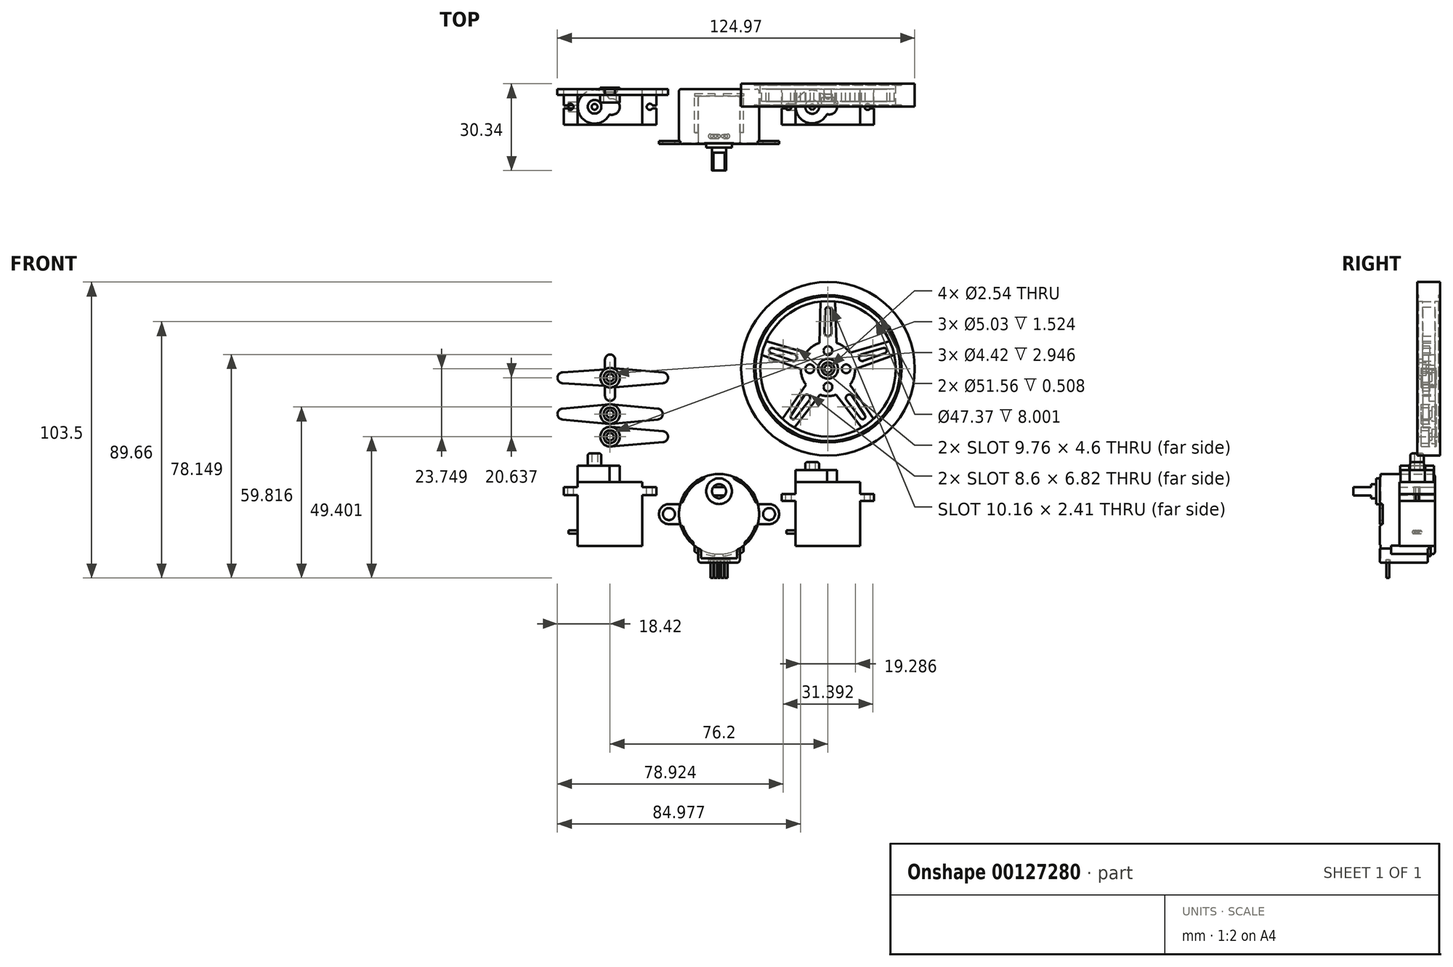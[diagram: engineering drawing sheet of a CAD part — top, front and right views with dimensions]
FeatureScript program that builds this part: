
annotation { "Feature Type Name" : "Feature", "Feature Type Description" : "" }
export const myFeature = defineFeature(function(context is Context, id is Id, definition is map)
    precondition{}
    {
        {
            var Q0;
            Q0=qCreatedBy(makeId("Front.planeOp"),FACE);
            var sketch = newSketch(context, id + "F0", { "sketchPlane" : qUnion([Q0])});
            skCircle(sketch, "E0", {"center": v(0, 0) * mm, "radius": 14 * mm});
            skSolve(sketch);
        }
        {
            var Q0;
            Q0=makeQuery(id+"F0.imprint","IMPRINT",FACE,{"disambiguationData":[TD([[makeQuery(id+"F0.imprint","IMPRINT",EDGE,{"derivedFrom":sQuery(id+"F0.wireOp",EDGE,"E0")}),1.0]])]});
            extrude(context, id + "F1", {"entities" : qUnion([Q0]), "depth" : 19 * mm});
        }
        {
            var Q0;
            Q0=makeQuery(id+"F1.opExtrude","CAP_EDGE",EDGE,{"disambiguationData":[OSD([sQuery(id+"F0.wireOp",EDGE,"E0")])],"isStart":true});
            fillet(context, id + "F2", {"entities" : qUnion([Q0]), "radius" : 0.8 * mm, "tangentPropagation" : true, "allowEdgeOverflow" : false});
        }
        {
            var Q0;
            Q0=makeQuery(id+"F1.opExtrude","CAP_FACE",FACE,{"disambiguationData":[OSD([sQuery(id+"F0.wireOp",EDGE,"E0")])],"isStart":false});
            var sketch = newSketch(context, id + "F3", { "sketchPlane" : qUnion([Q0])});
            skArc(sketch, "E1", {"start": v(12.7, 4.12) * mm, "mid": v(9.8, 9.06) * mm, "end": v(5.12, 12.33) * mm});
            skArc(sketch, "E2", {"start": v(-5.12, 12.33) * mm, "mid": v(-9.8, 9.06) * mm, "end": v(-12.7, 4.13) * mm});
            skLineSegment(sketch, "E3", {"start": v(-5.12, 12.33) * mm, "end": v(-5.12, 13.03) * mm});
            skLineSegment(sketch, "E4", {"start": v(-12.7, 4.12) * mm, "end": v(-13.38, 4.12) * mm});
            skLineSegment(sketch, "E5", {"start": v(12.7, 4.12) * mm, "end": v(13.38, 4.12) * mm});
            skLineSegment(sketch, "E6", {"start": v(5.12, 12.33) * mm, "end": v(5.12, 13.03) * mm});
            skArc(sketch, "E7", {"start": v(-12.7, -4.13) * mm, "mid": v(-11.22, -7.23) * mm, "end": v(-9, -9.86) * mm});
            skArc(sketch, "E8", {"start": v(9, -9.86) * mm, "mid": v(11.22, -7.23) * mm, "end": v(12.7, -4.12) * mm});
            skLineSegment(sketch, "E9", {"start": v(12.7, -4.12) * mm, "end": v(13.38, -4.12) * mm});
            skLineSegment(sketch, "E10", {"start": v(-12.7, -4.13) * mm, "end": v(-13.38, -4.13) * mm});
            skLineSegment(sketch, "E11", {"start": v(-9, -9.86) * mm, "end": v(-9, -10.72) * mm});
            skLineSegment(sketch, "E12", {"start": v(9, -9.86) * mm, "end": v(9, -10.72) * mm});
            skLineSegment(sketch, "E13", {"start": v(13.56, 3.5) * mm, "end": v(17.5, 3.5) * mm});
            skLineSegment(sketch, "E14", {"start": v(13.56, -3.5) * mm, "end": v(17.5, -3.5) * mm});
            skLineSegment(sketch, "E15", {"start": v(-13.56, 3.5) * mm, "end": v(-17.5, 3.5) * mm});
            skLineSegment(sketch, "E16", {"start": v(-13.56, -3.5) * mm, "end": v(-17.5, -3.5) * mm});
            skArc(sketch, "E17", {"start": v(17.5, -3.5) * mm, "mid": v(21, 0) * mm, "end": v(17.5, 3.5) * mm});
            skArc(sketch, "E18", {"start": v(-17.5, 3.5) * mm, "mid": v(-21, 0) * mm, "end": v(-17.5, -3.5) * mm});
            skCircle(sketch, "E19", {"center": v(-17.5, 0) * mm, "radius": 2.1 * mm});
            skCircle(sketch, "E20", {"center": v(17.5, 0) * mm, "radius": 2.1 * mm});
            skCircle(sketch, "E21", {"center": v(0, 8) * mm, "radius": 4.5 * mm});
            skSolve(sketch);
        }
        {
            var Q0;
            {var subQ1=sQuery(id+"F3.wireOp",EDGE,"E15");Q0=makeQuery(id+"F3.imprint","IMPRINT",FACE,{"disambiguationData":[TD([[makeQuery(id+"F3.imprint","IMPRINT",EDGE,{"derivedFrom":subQ1}),1.0]])]});}
            var Q1;
            {var subQ1=sQuery(id+"F3.wireOp",EDGE,"E13");Q1=makeQuery(id+"F3.imprint","IMPRINT",FACE,{"disambiguationData":[TD([[makeQuery(id+"F3.imprint","IMPRINT",EDGE,{"derivedFrom":subQ1}),-1.0]])]});}
            var Q2;
            Q2=makeQuery(id+"F3.imprint","IMPRINT",FACE,{"disambiguationData":[TD([[makeQuery(id+"F3.imprint","IMPRINT",EDGE,{"derivedFrom":sQuery(id+"F3.wireOp",EDGE,"E7")}),-1.0]])]});
            var Q3;
            Q3=makeQuery(id+"F3.imprint","IMPRINT",FACE,{"disambiguationData":[TD([[makeQuery(id+"F3.imprint","IMPRINT",EDGE,{"derivedFrom":sQuery(id+"F3.wireOp",EDGE,"E8")}),-1.0]])]});
            var Q4;
            Q4=makeQuery(id+"F3.imprint","IMPRINT",FACE,{"disambiguationData":[TD([[makeQuery(id+"F3.imprint","IMPRINT",EDGE,{"derivedFrom":sQuery(id+"F3.wireOp",EDGE,"E1")}),-1.0]])]});
            var Q5;
            Q5=makeQuery(id+"F3.imprint","IMPRINT",FACE,{"disambiguationData":[TD([[makeQuery(id+"F3.imprint","IMPRINT",EDGE,{"derivedFrom":sQuery(id+"F3.wireOp",EDGE,"E2")}),-1.0]])]});
            var Q6;
            Q6=makeQuery(id+"F3.imprint","IMPRINT",FACE,{"disambiguationData":[TD([[makeQuery(id+"F3.imprint","IMPRINT",EDGE,{"derivedFrom":sQuery(id+"F3.wireOp",EDGE,"E21")}),1.0]])]});
            extrude(context, id + "F4", {"entities" : qUnion([Q0, Q1, Q2, Q3, Q4, Q5, Q6]), "operationType" : NewBodyOperationType.ADD, "depth" : .25 * mm, "hasSecondDirection" : true, "secondDirectionOppositeDirection" : true, "secondDirectionDepth" : .8 * mm});
        }
        {
            var Q0;
            {var subQ0=sQuery(id+"F0.wireOp",EDGE,"E0");var subQ1=makeQuery(id+"F1.opExtrude","CAP_EDGE",EDGE,{"disambiguationData":[OSD([subQ0])],"isStart":false});Q0=makeQuery(id+"F4.opExtrude","CAP_EDGE",EDGE,{"disambiguationData":[OSD([subQ0]),TDD([makeQuery(id+"F3.imprint","IMPRINT",EDGE,{"disambiguationData":[TD([[makeQuery(id+"F3.imprint","INTERSECT",VERTEX,{"derivedFrom":[subQ1,sQuery(id+"F3.wireOp",EDGE,"E15")]}),-1.0]])],"derivedFrom":subQ1})])],"isStart":false});}
            var Q1;
            {var subQ0=sQuery(id+"F0.wireOp",EDGE,"E0");var subQ1=makeQuery(id+"F1.opExtrude","CAP_EDGE",EDGE,{"disambiguationData":[OSD([subQ0])],"isStart":false});Q1=makeQuery(id+"F4.opExtrude","CAP_EDGE",EDGE,{"disambiguationData":[OSD([subQ0]),TDD([makeQuery(id+"F3.imprint","IMPRINT",EDGE,{"disambiguationData":[TD([[makeQuery(id+"F3.imprint","INTERSECT",VERTEX,{"derivedFrom":[subQ1,sQuery(id+"F3.wireOp",EDGE,"E13")]}),1.0]])],"derivedFrom":subQ1})])],"isStart":false});}
            fillet(context, id + "F5", {"entities" : qUnion([Q0, Q1]), "radius" : 0.25 * mm, "tangentPropagation" : true, "allowEdgeOverflow" : false});
        }
        {
            var Q0;
            Q0=makeQuery(id+"F4.opExtrude","CAP_FACE",FACE,{"disambiguationData":[OSD([sQuery(id+"F3.wireOp",EDGE,"E21")])],"isStart":false});
            extrude(context, id + "F6", {"entities" : qUnion([Q0]), "operationType" : NewBodyOperationType.ADD, "depth" : 1.25 * mm});
        }
        {
            var Q0;
            Q0=makeQuery(id+"F1.opExtrude","CAP_FACE",FACE,{"disambiguationData":[OSD([sQuery(id+"F0.wireOp",EDGE,"E0")])],"isStart":false});
            var sketch = newSketch(context, id + "F7", { "sketchPlane" : qUnion([Q0])});
            skLineSegment(sketch, "E22", {"start": v(-7.25, -11.98) * mm, "end": v(-7.25, -16) * mm});
            skLineSegment(sketch, "E23", {"start": v(-6.25, -17) * mm, "end": v(6.25, -17) * mm});
            skLineSegment(sketch, "E24", {"start": v(7.25, -16) * mm, "end": v(7.25, -11.98) * mm});
            skPoint(sketch, "E25.visualSharp", {"position": v(-7.25, -17) * mm});
            skArc(sketch, "E25.filletArc", {"start": v(-7.25, -16) * mm, "mid": v(-6.96, -16.7) * mm, "end": v(-6.25, -17) * mm});
            skPoint(sketch, "E26.visualSharp", {"position": v(7.25, -17) * mm});
            skArc(sketch, "E26.filletArc", {"start": v(6.25, -17) * mm, "mid": v(6.96, -16.7) * mm, "end": v(7.25, -16) * mm});
            skLineSegment(sketch, "E27.0", {"start": v(-6.25, -15.5) * mm, "end": v(6.25, -15.5) * mm});
            skLineSegment(sketch, "E28.0", {"start": v(-6.25, -12.53) * mm, "end": v(-6.25, -15.5) * mm});
            skLineSegment(sketch, "E29.0", {"start": v(6.25, -15.5) * mm, "end": v(6.25, -12.53) * mm});
            skSolve(sketch);
        }
        {
            var Q0;
            Q0=makeQuery(id+"F7.imprint","IMPRINT",FACE,{"disambiguationData":[TD([[makeQuery(id+"F7.imprint","IMPRINT",EDGE,{"derivedFrom":sQuery(id+"F7.wireOp",EDGE,"E27.0")}),1.0]])]});
            var Q1;
            {var subQ2=sQuery(id+"F7.wireOp",EDGE,"E22");Q1=makeQuery(id+"F7.imprint","IMPRINT",FACE,{"disambiguationData":[TD([[makeQuery(id+"F7.imprint","IMPRINT",EDGE,{"derivedFrom":subQ2}),1.0]])]});}
            extrude(context, id + "F8", {"entities" : qUnion([Q0, Q1]), "operationType" : NewBodyOperationType.ADD, "oppositeDirection" : true, "depth" : 16.5 * mm});
        }
        {
            var Q0;
            {var subQ2=sQuery(id+"F7.wireOp",EDGE,"E22");Q0=makeQuery(id+"F7.imprint","IMPRINT",FACE,{"disambiguationData":[TD([[makeQuery(id+"F7.imprint","IMPRINT",EDGE,{"derivedFrom":subQ2}),1.0]])]});}
            extrude(context, id + "F9", {"entities" : qUnion([Q0]), "operationType" : NewBodyOperationType.ADD, "depth" : .25 * mm});
        }
        {
            var Q0;
            Q0=makeQuery(id+"F8.opExtrude","CAP_FACE",FACE,{"disambiguationData":[OSD([sQuery(id+"F0.wireOp",EDGE,"E0"),sQuery(id+"F7.wireOp",EDGE,"E22"),sQuery(id+"F7.wireOp",EDGE,"E23"),sQuery(id+"F7.wireOp",EDGE,"E24"),sQuery(id+"F7.wireOp",EDGE,"E25.filletArc"),sQuery(id+"F7.wireOp",EDGE,"E26.filletArc")])],"isStart":false});
            var sketch = newSketch(context, id + "F10", { "sketchPlane" : qUnion([Q0])});
            skCircle(sketch, "E30.0", {"center": v(0, 0) * mm, "radius": 14 * mm});
            skLineSegment(sketch, "E31", {"start": v(8.6, -11.05) * mm, "end": v(8.6, -13.05) * mm});
            skLineSegment(sketch, "E32", {"start": v(8.6, -13.05) * mm, "end": v(7.25, -14) * mm});
            skLineSegment(sketch, "E33", {"start": v(-8.6, -11.05) * mm, "end": v(-8.6, -13.05) * mm});
            skLineSegment(sketch, "E34", {"start": v(-8.6, -13.05) * mm, "end": v(-7.25, -14) * mm});
            skPoint(sketch, "E34.endSnap0", {"position": v(-7.25, -13.99) * mm});
            skArc(sketch, "E35", {"start": v(-8.6, -11.98) * mm, "mid": v(-5.23, -13.8) * mm, "end": v(-1.5, -14.67) * mm});
            skArc(sketch, "E36", {"start": v(1.5, -14.67) * mm, "mid": v(5.23, -13.8) * mm, "end": v(8.6, -11.98) * mm});
            skLineSegment(sketch, "E37", {"start": v(-1.5, -14.67) * mm, "end": v(-1.5, -13.92) * mm});
            skLineSegment(sketch, "E38", {"start": v(1.5, -14.67) * mm, "end": v(1.5, -13.92) * mm});
            skSolve(sketch);
        }
        {
            var Q0;
            {var subQ0=sQuery(id+"F10.wireOp",EDGE,"E34");Q0=makeQuery(id+"F10.imprint","IMPRINT",FACE,{"disambiguationData":[TD([[makeQuery(id+"F10.imprint","IMPRINT",EDGE,{"derivedFrom":subQ0}),1.0]])]});}
            var Q1;
            {var subQ0=sQuery(id+"F10.wireOp",EDGE,"E30.0");var subQ3=sQuery(id+"F10.wireOp",EDGE,"E33");var subQ4=makeQuery(id+"F10.imprint","INTERSECT",VERTEX,{"derivedFrom":[subQ0,subQ3]});Q1=makeQuery(id+"F10.imprint","IMPRINT",FACE,{"disambiguationData":[TD([[makeQuery(id+"F10.imprint","IMPRINT",EDGE,{"disambiguationData":[TD([[subQ4,-1.0]])],"derivedFrom":subQ0}),-1.0]])]});}
            var Q2;
            {var subQ0=sQuery(id+"F10.wireOp",EDGE,"E32");Q2=makeQuery(id+"F10.imprint","IMPRINT",FACE,{"disambiguationData":[TD([[makeQuery(id+"F10.imprint","IMPRINT",EDGE,{"derivedFrom":subQ0}),-1.0]])]});}
            var Q3;
            {var subQ0=sQuery(id+"F10.wireOp",EDGE,"E30.0");var subQ3=sQuery(id+"F10.wireOp",EDGE,"E31");var subQ4=makeQuery(id+"F10.imprint","INTERSECT",VERTEX,{"derivedFrom":[subQ0,subQ3]});Q3=makeQuery(id+"F10.imprint","IMPRINT",FACE,{"disambiguationData":[TD([[makeQuery(id+"F10.imprint","IMPRINT",EDGE,{"disambiguationData":[TD([[subQ4,1.0]])],"derivedFrom":subQ0}),-1.0]])]});}
            extrude(context, id + "F11", {"entities" : qUnion([Q0, Q1, Q2, Q3]), "operationType" : NewBodyOperationType.ADD, "oppositeDirection" : true, "depth" : 12.75 * mm});
        }
        {
            var Q0;
            {var subQ3=sQuery(id+"F10.wireOp",EDGE,"E37");Q0=makeQuery(id+"F10.imprint","IMPRINT",FACE,{"disambiguationData":[TD([[makeQuery(id+"F10.imprint","IMPRINT",EDGE,{"derivedFrom":subQ3}),1.0]])]});}
            var Q1;
            {var subQ0=sQuery(id+"F10.wireOp",EDGE,"E30.0");var subQ3=sQuery(id+"F10.wireOp",EDGE,"E33");var subQ4=makeQuery(id+"F10.imprint","INTERSECT",VERTEX,{"derivedFrom":[subQ0,subQ3]});Q1=makeQuery(id+"F10.imprint","IMPRINT",FACE,{"disambiguationData":[TD([[makeQuery(id+"F10.imprint","IMPRINT",EDGE,{"disambiguationData":[TD([[subQ4,-1.0]])],"derivedFrom":subQ0}),-1.0]])]});}
            var Q2;
            {var subQ3=sQuery(id+"F10.wireOp",EDGE,"E38");Q2=makeQuery(id+"F10.imprint","IMPRINT",FACE,{"disambiguationData":[TD([[makeQuery(id+"F10.imprint","IMPRINT",EDGE,{"derivedFrom":subQ3}),-1.0]])]});}
            var Q3;
            {var subQ0=sQuery(id+"F10.wireOp",EDGE,"E30.0");var subQ3=sQuery(id+"F10.wireOp",EDGE,"E31");var subQ4=makeQuery(id+"F10.imprint","INTERSECT",VERTEX,{"derivedFrom":[subQ0,subQ3]});Q3=makeQuery(id+"F10.imprint","IMPRINT",FACE,{"disambiguationData":[TD([[makeQuery(id+"F10.imprint","IMPRINT",EDGE,{"disambiguationData":[TD([[subQ4,1.0]])],"derivedFrom":subQ0}),-1.0]])]});}
            extrude(context, id + "F12", {"entities" : qUnion([Q0, Q1, Q2, Q3]), "operationType" : NewBodyOperationType.ADD, "depth" : 1 * mm});
        }
        {
            var Q0;
            Q0=makeQuery(id+"F11.opExtrude","SWEPT_EDGE",EDGE,{"disambiguationData":[OSD([sQuery(id+"F10.wireOp",EDGE,"E33"),sQuery(id+"F10.wireOp",EDGE,"E34")])]});
            var Q1;
            Q1=makeQuery(id+"F11.opExtrude","SWEPT_EDGE",EDGE,{"disambiguationData":[OSD([sQuery(id+"F10.wireOp",EDGE,"E31"),sQuery(id+"F10.wireOp",EDGE,"E32")])]});
            var Q2;
            Q2=makeQuery(id+"F8.opExtrude","CAP_EDGE",EDGE,{"disambiguationData":[OSD([sQuery(id+"F7.wireOp",EDGE,"E23")])],"isStart":false});
            var Q3;
            Q3=makeQuery(id+"F9.opExtrude","CAP_EDGE",EDGE,{"disambiguationData":[OSD([sQuery(id+"F7.wireOp",EDGE,"E23")])],"isStart":false});
            fillet(context, id + "F13", {"entities" : qUnion([Q0, Q1, Q2, Q3]), "radius" : .5 * mm, "tangentPropagation" : true, "allowEdgeOverflow" : false});
        }
        {
            var Q0;
            Q0=makeQuery(id+"F6.opExtrude","CAP_FACE",FACE,{"disambiguationData":[OSD([sQuery(id+"F3.wireOp",EDGE,"E21")])],"isStart":false});
            var sketch = newSketch(context, id + "F14", { "sketchPlane" : qUnion([Q0])});
            skCircle(sketch, "E39", {"center": v(0, 8) * mm, "radius": 2.48 * mm});
            skLineSegment(sketch, "E40", {"start": v(-1.99, 9.48) * mm, "end": v(1.99, 9.48) * mm});
            skLineSegment(sketch, "E41", {"start": v(-1.99, 6.53) * mm, "end": v(1.99, 6.53) * mm});
            skSolve(sketch);
        }
        {
            var Q0;
            Q0=makeQuery(id+"F14.imprint","IMPRINT",FACE,{"disambiguationData":[TD([[makeQuery(id+"F14.imprint","IMPRINT",EDGE,{"derivedFrom":sQuery(id+"F14.wireOp",EDGE,"E39")}),1.0]])]});
            var Q1;
            {var subQ0=sQuery(id+"F14.wireOp",EDGE,"E41");Q1=makeQuery(id+"F14.imprint","IMPRINT",FACE,{"disambiguationData":[TD([[makeQuery(id+"F14.imprint","IMPRINT",EDGE,{"derivedFrom":subQ0}),-1.0]])]});}
            var Q2;
            {var subQ0=sQuery(id+"F14.wireOp",EDGE,"E40");Q2=makeQuery(id+"F14.imprint","IMPRINT",FACE,{"disambiguationData":[TD([[makeQuery(id+"F14.imprint","IMPRINT",EDGE,{"derivedFrom":subQ0}),1.0]])]});}
            extrude(context, id + "F15", {"entities" : qUnion([Q0, Q1, Q2]), "operationType" : NewBodyOperationType.ADD, "depth" : 1.75 * mm});
        }
        {
            var Q0;
            {var subQ0=sQuery(id+"F14.wireOp",EDGE,"E40");Q0=makeQuery(id+"F14.imprint","IMPRINT",FACE,{"disambiguationData":[TD([[makeQuery(id+"F14.imprint","IMPRINT",EDGE,{"derivedFrom":subQ0}),-1.0]])]});}
            extrude(context, id + "F16", {"entities" : qUnion([Q0]), "operationType" : NewBodyOperationType.ADD, "depth" : 8 * mm});
        }
        {
            var Q0;
            {var subQ0=sQuery(id+"F7.wireOp",EDGE,"E23");Q0=makeQuery(id+"F9.boolean.opBoolean","MERGE",FACE,{"derivedFrom":[makeQuery(id+"F8.opExtrude","SWEPT_FACE",FACE,{"disambiguationData":[OSD([subQ0])]}),makeQuery(id+"F9.opExtrude","SWEPT_FACE",FACE,{"disambiguationData":[OSD([subQ0])]})]});}
            var sketch = newSketch(context, id + "F17", { "sketchPlane" : qUnion([Q0])});
            skLineSegment(sketch, "E42", {"start": v(-3, 15.75) * mm, "end": v(3, 15.75) * mm});
            skLineSegment(sketch, "E43", {"start": v(-3, 17.25) * mm, "end": v(3, 17.25) * mm});
            skArc(sketch, "E44", {"start": v(-3, 17.25) * mm, "mid": v(-3.75, 16.5) * mm, "end": v(-3, 15.75) * mm});
            skArc(sketch, "E45", {"start": v(3, 15.75) * mm, "mid": v(3.75, 16.5) * mm, "end": v(3, 17.25) * mm});
            skLineSegment(sketch, "E46", {"start": v(-3, 16.5) * mm, "end": v(3, 16.5) * mm, "construction": true});
            skPoint(sketch, "E47", {"position": v(0, 16.5) * mm});
            skSolve(sketch);
        }
        {
            var Q0;
            Q0=makeQuery(id+"F17.imprint","IMPRINT",FACE,{"disambiguationData":[TD([[makeQuery(id+"F17.imprint","IMPRINT",EDGE,{"derivedFrom":sQuery(id+"F17.wireOp",EDGE,"E42")}),1.0]])]});
            extrude(context, id + "F18", {"entities" : qUnion([Q0]), "operationType" : NewBodyOperationType.REMOVE, "oppositeDirection" : true, "depth" : 1 * mm});
        }
        {
            var Q0;
            Q0=makeQuery(id+"F18.boolean.opBoolean","COPY",FACE,{"derivedFrom":makeQuery(id+"F18.opExtrude","CAP_FACE",FACE,{"disambiguationData":[OSD([sQuery(id+"F17.wireOp",EDGE,"E42"),sQuery(id+"F17.wireOp",EDGE,"E43"),sQuery(id+"F17.wireOp",EDGE,"E44"),sQuery(id+"F17.wireOp",EDGE,"E45")])],"isStart":false})});
            var sketch = newSketch(context, id + "F19", { "sketchPlane" : qUnion([Q0])});
            skLineSegment(sketch, "E48", {"start": v(-3, 16.5) * mm, "end": v(3, 16.5) * mm, "construction": true});
            skCircle(sketch, "E49", {"center": v(-2.5, 16.5) * mm, "radius": 0.5 * mm});
            skCircle(sketch, "E50", {"center": v(2.5, 16.5) * mm, "radius": 0.5 * mm});
            skCircle(sketch, "E51", {"center": v(0, 16.5) * mm, "radius": 0.5 * mm});
            skLineSegment(sketch, "E52", {"start": v(-2.5, 16.5) * mm, "end": v(0, 16.5) * mm, "construction": true});
            skLineSegment(sketch, "E53", {"start": v(0, 16.5) * mm, "end": v(2.5, 16.5) * mm, "construction": true});
            skCircle(sketch, "E54", {"center": v(-1.25, 16.5) * mm, "radius": 0.5 * mm});
            skCircle(sketch, "E55", {"center": v(1.25, 16.5) * mm, "radius": 0.5 * mm});
            skSolve(sketch);
        }
        {
            var Q0;
            Q0=makeQuery(id+"F19.imprint","IMPRINT",FACE,{"disambiguationData":[TD([[makeQuery(id+"F19.imprint","IMPRINT",EDGE,{"derivedFrom":sQuery(id+"F19.wireOp",EDGE,"E49")}),1.0]])]});
            var Q1;
            Q1=makeQuery(id+"F19.imprint","IMPRINT",FACE,{"disambiguationData":[TD([[makeQuery(id+"F19.imprint","IMPRINT",EDGE,{"derivedFrom":sQuery(id+"F19.wireOp",EDGE,"E54")}),1.0]])]});
            var Q2;
            Q2=makeQuery(id+"F19.imprint","IMPRINT",FACE,{"disambiguationData":[TD([[makeQuery(id+"F19.imprint","IMPRINT",EDGE,{"derivedFrom":sQuery(id+"F19.wireOp",EDGE,"E51")}),1.0]])]});
            var Q3;
            Q3=makeQuery(id+"F19.imprint","IMPRINT",FACE,{"disambiguationData":[TD([[makeQuery(id+"F19.imprint","IMPRINT",EDGE,{"derivedFrom":sQuery(id+"F19.wireOp",EDGE,"E55")}),1.0]])]});
            var Q4;
            Q4=makeQuery(id+"F19.imprint","IMPRINT",FACE,{"disambiguationData":[TD([[makeQuery(id+"F19.imprint","IMPRINT",EDGE,{"derivedFrom":sQuery(id+"F19.wireOp",EDGE,"E50")}),1.0]])]});
            extrude(context, id + "F20", {"entities" : qUnion([Q0, Q1, Q2, Q3, Q4]), "operationType" : NewBodyOperationType.ADD, "depth" : 6.35 * mm});
        }
        {
            var Q0;
            Q0=qCreatedBy(makeId("Front.planeOp"),FACE);
            var sketch = newSketch(context, id + "F21", { "sketchPlane" : qUnion([Q0])});
            skLineSegment(sketch, "E56.bottom", {"start": v(26.8, -11.18) * mm, "end": v(49.4, -11.18) * mm});
            skLineSegment(sketch, "E56.top", {"start": v(26.8, 11.18) * mm, "end": v(49.4, 11.18) * mm});
            skLineSegment(sketch, "E56.left", {"start": v(26.8, -11.18) * mm, "end": v(26.8, 11.18) * mm});
            skLineSegment(sketch, "E56.right", {"start": v(49.4, -11.18) * mm, "end": v(49.4, 11.18) * mm});
            skPoint(sketch, "E56.middle", {"position": v(38.1, 0) * mm});
            skLineSegment(sketch, "E57.bottom", {"start": v(21.97, 4.57) * mm, "end": v(54.23, 4.57) * mm});
            skLineSegment(sketch, "E57.top", {"start": v(21.97, 6.99) * mm, "end": v(54.23, 6.99) * mm});
            skLineSegment(sketch, "E57.left", {"start": v(21.97, 4.57) * mm, "end": v(21.97, 6.99) * mm});
            skLineSegment(sketch, "E57.right", {"start": v(54.23, 4.57) * mm, "end": v(54.23, 6.99) * mm});
            skPoint(sketch, "E57.middle", {"position": v(38.1, 5.78) * mm});
            skLineSegment(sketch, "E58.bottom", {"start": v(-26.8, -11.18) * mm, "end": v(-49.4, -11.18) * mm});
            skLineSegment(sketch, "E58.top", {"start": v(-26.8, 11.18) * mm, "end": v(-49.4, 11.18) * mm});
            skLineSegment(sketch, "E58.left", {"start": v(-26.8, -11.18) * mm, "end": v(-26.8, 11.18) * mm});
            skLineSegment(sketch, "E58.right", {"start": v(-49.4, -11.18) * mm, "end": v(-49.4, 11.18) * mm});
            skPoint(sketch, "E58.middle", {"position": v(-38.1, 0) * mm});
            skLineSegment(sketch, "E59.bottom", {"start": v(-54.27, 6.68) * mm, "end": v(-21.93, 6.68) * mm});
            skLineSegment(sketch, "E59.top", {"start": v(-54.27, 9.4) * mm, "end": v(-21.93, 9.4) * mm});
            skLineSegment(sketch, "E59.left", {"start": v(-54.27, 6.68) * mm, "end": v(-54.27, 9.4) * mm});
            skLineSegment(sketch, "E59.right", {"start": v(-21.93, 6.68) * mm, "end": v(-21.93, 9.4) * mm});
            skPoint(sketch, "E59.middle", {"position": v(-38.1, 8.04) * mm});
            skSolve(sketch);
        }
        {
            var Q0;
            {var subQ0=sQuery(id+"F21.wireOp",EDGE,"E56.top");Q0=makeQuery(id+"F21.imprint","IMPRINT",FACE,{"disambiguationData":[TD([[makeQuery(id+"F21.imprint","IMPRINT",EDGE,{"derivedFrom":subQ0}),-1.0]])]});}
            var Q1;
            {var subQ0=sQuery(id+"F21.wireOp",EDGE,"E57.bottom");var subQ1=sQuery(id+"F21.wireOp",EDGE,"E56.left");var subQ2=makeQuery(id+"F21.imprint","INTERSECT",VERTEX,{"derivedFrom":[subQ1,subQ0]});Q1=makeQuery(id+"F21.imprint","IMPRINT",FACE,{"disambiguationData":[TD([[makeQuery(id+"F21.imprint","IMPRINT",EDGE,{"disambiguationData":[TD([[subQ2,-1.0]])],"derivedFrom":subQ1}),-1.0]])]});}
            var Q2;
            {var subQ5=sQuery(id+"F21.wireOp",EDGE,"E57.left");Q2=makeQuery(id+"F21.imprint","IMPRINT",FACE,{"disambiguationData":[TD([[makeQuery(id+"F21.imprint","IMPRINT",EDGE,{"derivedFrom":subQ5}),-1.0]])]});}
            var Q3;
            {var subQ0=sQuery(id+"F21.wireOp",EDGE,"E56.bottom");Q3=makeQuery(id+"F21.imprint","IMPRINT",FACE,{"disambiguationData":[TD([[makeQuery(id+"F21.imprint","IMPRINT",EDGE,{"derivedFrom":subQ0}),1.0]])]});}
            var Q4;
            {var subQ5=sQuery(id+"F21.wireOp",EDGE,"E57.right");Q4=makeQuery(id+"F21.imprint","IMPRINT",FACE,{"disambiguationData":[TD([[makeQuery(id+"F21.imprint","IMPRINT",EDGE,{"derivedFrom":subQ5}),1.0]])]});}
            var Q5;
            {var subQ0=sQuery(id+"F21.wireOp",EDGE,"E58.bottom");Q5=makeQuery(id+"F21.imprint","IMPRINT",FACE,{"disambiguationData":[TD([[makeQuery(id+"F21.imprint","IMPRINT",EDGE,{"derivedFrom":subQ0}),-1.0]])]});}
            var Q6;
            {var subQ0=sQuery(id+"F21.wireOp",EDGE,"E59.bottom");var subQ1=sQuery(id+"F21.wireOp",EDGE,"E58.left");var subQ2=makeQuery(id+"F21.imprint","INTERSECT",VERTEX,{"derivedFrom":[subQ1,subQ0]});Q6=makeQuery(id+"F21.imprint","IMPRINT",FACE,{"disambiguationData":[TD([[makeQuery(id+"F21.imprint","IMPRINT",EDGE,{"disambiguationData":[TD([[subQ2,-1.0]])],"derivedFrom":subQ1}),1.0]])]});}
            var Q7;
            {var subQ5=sQuery(id+"F21.wireOp",EDGE,"E59.right");Q7=makeQuery(id+"F21.imprint","IMPRINT",FACE,{"disambiguationData":[TD([[makeQuery(id+"F21.imprint","IMPRINT",EDGE,{"derivedFrom":subQ5}),1.0]])]});}
            var Q8;
            {var subQ5=sQuery(id+"F21.wireOp",EDGE,"E59.left");Q8=makeQuery(id+"F21.imprint","IMPRINT",FACE,{"disambiguationData":[TD([[makeQuery(id+"F21.imprint","IMPRINT",EDGE,{"derivedFrom":subQ5}),-1.0]])]});}
            var Q9;
            {var subQ0=sQuery(id+"F21.wireOp",EDGE,"E58.top");Q9=makeQuery(id+"F21.imprint","IMPRINT",FACE,{"disambiguationData":[TD([[makeQuery(id+"F21.imprint","IMPRINT",EDGE,{"derivedFrom":subQ0}),1.0]])]});}
            extrude(context, id + "F22", {"entities" : qUnion([Q0, Q1, Q2, Q3, Q4, Q5, Q6, Q7, Q8, Q9]), "depth" : 12.45 * mm});
        }
        {
            var Q0;
            {var subQ0=sQuery(id+"F21.wireOp",EDGE,"E57.top");Q0=makeQuery(id+"F22.opExtrude","SWEPT_FACE",FACE,{"disambiguationData":[OSD([subQ0]),TDD([makeQuery(id+"F21.imprint","IMPRINT",EDGE,{"disambiguationData":[TD([[makeQuery(id+"F21.imprint","INTERSECT",VERTEX,{"derivedFrom":[subQ0,sQuery(id+"F21.wireOp",EDGE,"E57.left")]}),-1.0]])],"derivedFrom":subQ0})])]});}
            var sketch = newSketch(context, id + "F23", { "sketchPlane" : qUnion([Q0])});
            skLineSegment(sketch, "E60.0.0", {"start": v(54.23, 0) * mm, "end": v(49.4, 0) * mm, "construction": true});
            skLineSegment(sketch, "E60.0.1", {"start": v(49.4, 0) * mm, "end": v(49.4, -12.45) * mm, "construction": true});
            skLineSegment(sketch, "E60.0.2", {"start": v(49.4, -12.45) * mm, "end": v(54.23, -12.45) * mm, "construction": true});
            skLineSegment(sketch, "E60.0.3", {"start": v(54.23, -12.45) * mm, "end": v(54.23, 0) * mm, "construction": true});
            skArc(sketch, "E61", {"start": v(23.3, -6.73) * mm, "mid": v(25.34, -6.22) * mm, "end": v(23.3, -5.71) * mm});
            skPoint(sketch, "E61.centerSnap0", {"position": v(26.8, -6.22) * mm});
            skArc(sketch, "E62", {"start": v(52.9, -5.72) * mm, "mid": v(50.86, -6.22) * mm, "end": v(52.9, -6.73) * mm});
            skPoint(sketch, "E62.centerSnap0", {"position": v(54.23, -6.22) * mm});
            skLineSegment(sketch, "E63", {"start": v(23.3, -5.71) * mm, "end": v(21.97, -5.71) * mm});
            skLineSegment(sketch, "E64", {"start": v(23.3, -6.73) * mm, "end": v(21.97, -6.73) * mm});
            skLineSegment(sketch, "E65", {"start": v(52.9, -5.72) * mm, "end": v(54.23, -5.72) * mm});
            skLineSegment(sketch, "E66", {"start": v(54.23, -5.72) * mm, "end": v(54.23, -6.73) * mm});
            skLineSegment(sketch, "E67", {"start": v(54.23, -6.73) * mm, "end": v(52.9, -6.73) * mm});
            skSolve(sketch);
        }
        {
            var Q0;
            Q0=makeQuery(id+"F23.imprint","IMPRINT",FACE,{"disambiguationData":[TD([[makeQuery(id+"F23.imprint","IMPRINT",EDGE,{"derivedFrom":sQuery(id+"F23.wireOp",EDGE,"E61")}),1.0]])]});
            var Q1;
            Q1=makeQuery(id+"F23.imprint","IMPRINT",FACE,{"disambiguationData":[TD([[makeQuery(id+"F23.imprint","IMPRINT",EDGE,{"derivedFrom":sQuery(id+"F23.wireOp",EDGE,"E62")}),1.0]])]});
            extrude(context, id + "F24", {"entities" : qUnion([Q0, Q1]), "operationType" : NewBodyOperationType.REMOVE, "oppositeDirection" : true, "depth" : 3.17 * mm});
        }
        {
            var Q0;
            Q0=makeQuery(id+"F22.opExtrude","SWEPT_FACE",FACE,{"disambiguationData":[OSD([sQuery(id+"F21.wireOp",EDGE,"E56.top")])]});
            var sketch = newSketch(context, id + "F25", { "sketchPlane" : qUnion([Q0])});
            skCircle(sketch, "E68", {"center": v(32.58, -6.22) * mm, "radius": 5.78 * mm});
            skArc(sketch, "E69", {"start": v(37.77, -8.75) * mm, "mid": v(41.27, -6.22) * mm, "end": v(37.77, -3.7) * mm});
            skPoint(sketch, "E70", {"position": v(26.8, -6.22) * mm});
            skLineSegment(sketch, "E71.0", {"start": v(-49.4, -12.45) * mm, "end": v(-49.4, 0) * mm, "construction": true});
            skCircle(sketch, "E72", {"center": v(-43.52, -6.22) * mm, "radius": 5.88 * mm});
            skPoint(sketch, "E72.centerSnap0", {"position": v(-49.4, -6.22) * mm});
            skArc(sketch, "E73", {"start": v(-38.3, -8.9) * mm, "mid": v(-34.72, -6.22) * mm, "end": v(-38.3, -3.54) * mm});
            skSolve(sketch);
        }
        {
            var Q0;
            {var subQ0=sQuery(id+"F25.wireOp",EDGE,"E69");var subQ1=sQuery(id+"F25.wireOp",EDGE,"E68");var subQ4=makeQuery(id+"F25.imprint","INTERSECT",VERTEX,{"disambiguationData":[OD(0.0)],"derivedFrom":[subQ1,subQ0]});Q0=makeQuery(id+"F25.imprint","IMPRINT",FACE,{"disambiguationData":[TD([[makeQuery(id+"F25.imprint","IMPRINT",EDGE,{"disambiguationData":[TD([[subQ4,-1.0]])],"derivedFrom":subQ1}),1.0]])]});}
            var Q1;
            {var subQ0=sQuery(id+"F25.wireOp",EDGE,"E69");Q1=makeQuery(id+"F25.imprint","IMPRINT",FACE,{"disambiguationData":[TD([[makeQuery(id+"F25.imprint","IMPRINT",EDGE,{"derivedFrom":subQ0}),1.0]])]});}
            extrude(context, id + "F26", {"entities" : qUnion([Q0, Q1]), "operationType" : NewBodyOperationType.ADD, "depth" : 4.22 * mm});
        }
        {
            var Q0;
            Q0=makeQuery(id+"F26.opExtrude","CAP_FACE",FACE,{"disambiguationData":[OSD([sQuery(id+"F25.wireOp",EDGE,"E68"),sQuery(id+"F25.wireOp",EDGE,"E69")])],"isStart":false});
            var sketch = newSketch(context, id + "F27", { "sketchPlane" : qUnion([Q0])});
            skCircle(sketch, "E74", {"center": v(32.58, -6.22) * mm, "radius": 2.44 * mm});
            skCircle(sketch, "E75", {"center": v(32.58, -6.22) * mm, "radius": 1 * mm});
            skSolve(sketch);
        }
        {
            var Q0;
            Q0=makeQuery(id+"F27.imprint","IMPRINT",FACE,{"disambiguationData":[TD([[makeQuery(id+"F27.imprint","IMPRINT",EDGE,{"derivedFrom":sQuery(id+"F27.wireOp",EDGE,"E74")}),1.0]])]});
            extrude(context, id + "F28", {"entities" : qUnion([Q0]), "operationType" : NewBodyOperationType.ADD, "depth" : 2.8 * mm});
        }
        {
            var Q0;
            {var subQ0=sQuery(id+"F21.wireOp",EDGE,"E56.left");Q0=makeQuery(id+"F22.opExtrude","SWEPT_FACE",FACE,{"disambiguationData":[OSD([subQ0]),TDD([makeQuery(id+"F21.imprint","IMPRINT",EDGE,{"disambiguationData":[TD([[makeQuery(id+"F21.imprint","INTERSECT",VERTEX,{"derivedFrom":[sQuery(id+"F21.wireOp",EDGE,"E56.bottom"),subQ0]}),-1.0]])],"derivedFrom":subQ0})])]});}
            var sketch = newSketch(context, id + "F29", { "sketchPlane" : qUnion([Q0])});
            skCircle(sketch, "E76", {"center": v(6.8, -6.3) * mm, "radius": 0.56 * mm});
            skCircle(sketch, "E77", {"center": v(5.65, -6.3) * mm, "radius": 0.56 * mm});
            skLineSegment(sketch, "E78", {"start": v(5.65, -6.3) * mm, "end": v(6.8, -6.3) * mm, "construction": true});
            skPoint(sketch, "E79", {"position": v(6.22, -11.18) * mm});
            skPoint(sketch, "E80", {"position": v(6.22, -6.3) * mm});
            skSolve(sketch);
        }
        {
            var Q0;
            Q0=makeQuery(id+"F29.imprint","IMPRINT",FACE,{"disambiguationData":[TD([[makeQuery(id+"F29.imprint","IMPRINT",EDGE,{"derivedFrom":sQuery(id+"F29.wireOp",EDGE,"E77")}),1.0]])]});
            var Q1;
            Q1=makeQuery(id+"F29.imprint","IMPRINT",FACE,{"disambiguationData":[TD([[makeQuery(id+"F29.imprint","IMPRINT",EDGE,{"derivedFrom":sQuery(id+"F29.wireOp",EDGE,"E76")}),1.0]])]});
            extrude(context, id + "F30", {"entities" : qUnion([Q0, Q1]), "operationType" : NewBodyOperationType.ADD, "depth" : 3.17 * mm});
        }
        {
            var Q0;
            {var subQ0=sQuery(id+"F21.wireOp",EDGE,"E59.top");Q0=makeQuery(id+"F22.opExtrude","SWEPT_FACE",FACE,{"disambiguationData":[OSD([subQ0]),TDD([makeQuery(id+"F21.imprint","IMPRINT",EDGE,{"disambiguationData":[TD([[makeQuery(id+"F21.imprint","INTERSECT",VERTEX,{"derivedFrom":[subQ0,sQuery(id+"F21.wireOp",EDGE,"E59.left")]}),-1.0]])],"derivedFrom":subQ0})])]});}
            var sketch = newSketch(context, id + "F31", { "sketchPlane" : qUnion([Q0])});
            skArc(sketch, "E81", {"start": v(-52.93, -6.73) * mm, "mid": v(-50.9, -6.22) * mm, "end": v(-52.93, -5.72) * mm});
            skPoint(sketch, "E81.centerSnap0", {"position": v(-49.4, -6.22) * mm});
            skArc(sketch, "E82", {"start": v(-23.27, -5.72) * mm, "mid": v(-25.3, -6.22) * mm, "end": v(-23.27, -6.73) * mm});
            skPoint(sketch, "E82.centerSnap0", {"position": v(-21.93, -6.22) * mm});
            skLineSegment(sketch, "E83", {"start": v(-52.93, -5.72) * mm, "end": v(-54.27, -5.72) * mm});
            skLineSegment(sketch, "E84", {"start": v(-52.93, -6.73) * mm, "end": v(-54.27, -6.73) * mm});
            skLineSegment(sketch, "E85", {"start": v(-23.27, -5.72) * mm, "end": v(-21.93, -5.72) * mm});
            skLineSegment(sketch, "E86", {"start": v(-21.93, -5.72) * mm, "end": v(-21.93, -6.73) * mm});
            skLineSegment(sketch, "E87", {"start": v(-21.93, -6.73) * mm, "end": v(-23.27, -6.73) * mm});
            skLineSegment(sketch, "E88.0.0", {"start": v(-21.93, 0) * mm, "end": v(-26.8, 0) * mm, "construction": true});
            skLineSegment(sketch, "E88.0.1", {"start": v(-26.8, 0) * mm, "end": v(-26.8, -12.45) * mm, "construction": true});
            skLineSegment(sketch, "E88.0.2", {"start": v(-26.8, -12.45) * mm, "end": v(-21.93, -12.45) * mm, "construction": true});
            skLineSegment(sketch, "E88.0.3", {"start": v(-21.93, -12.45) * mm, "end": v(-21.93, 0) * mm, "construction": true});
            skSolve(sketch);
        }
        {
            var Q0;
            Q0=makeQuery(id+"F31.imprint","IMPRINT",FACE,{"disambiguationData":[TD([[makeQuery(id+"F31.imprint","IMPRINT",EDGE,{"derivedFrom":sQuery(id+"F31.wireOp",EDGE,"E81")}),1.0]])]});
            var Q1;
            Q1=makeQuery(id+"F31.imprint","IMPRINT",FACE,{"disambiguationData":[TD([[makeQuery(id+"F31.imprint","IMPRINT",EDGE,{"derivedFrom":sQuery(id+"F31.wireOp",EDGE,"E82")}),1.0]])]});
            extrude(context, id + "F32", {"entities" : qUnion([Q0, Q1]), "operationType" : NewBodyOperationType.REMOVE, "oppositeDirection" : true, "depth" : 3.17 * mm});
        }
        {
            var Q0;
            {var subQ0=sQuery(id+"F25.wireOp",EDGE,"E73");var subQ1=sQuery(id+"F25.wireOp",EDGE,"E72");var subQ2=makeQuery(id+"F25.imprint","INTERSECT",VERTEX,{"disambiguationData":[OD(0.0)],"derivedFrom":[subQ1,subQ0]});Q0=makeQuery(id+"F25.imprint","IMPRINT",FACE,{"disambiguationData":[TD([[makeQuery(id+"F25.imprint","IMPRINT",EDGE,{"disambiguationData":[TD([[subQ2,1.0]])],"derivedFrom":subQ1}),1.0]])]});}
            var Q1;
            {var subQ0=sQuery(id+"F25.wireOp",EDGE,"E73");Q1=makeQuery(id+"F25.imprint","IMPRINT",FACE,{"disambiguationData":[TD([[makeQuery(id+"F25.imprint","IMPRINT",EDGE,{"derivedFrom":subQ0}),1.0]])]});}
            extrude(context, id + "F33", {"entities" : qUnion([Q0, Q1]), "operationType" : NewBodyOperationType.ADD, "depth" : 5.74 * mm});
        }
        {
            var Q0;
            Q0=makeQuery(id+"F33.opExtrude","CAP_FACE",FACE,{"disambiguationData":[OSD([sQuery(id+"F25.wireOp",EDGE,"E72"),sQuery(id+"F25.wireOp",EDGE,"E73")])],"isStart":false});
            var sketch = newSketch(context, id + "F34", { "sketchPlane" : qUnion([Q0])});
            skCircle(sketch, "E89", {"center": v(-43.52, -6.22) * mm, "radius": 2.37 * mm});
            skCircle(sketch, "E90", {"center": v(-43.52, -6.22) * mm, "radius": 1.02 * mm});
            skSolve(sketch);
        }
        {
            var Q0;
            Q0=makeQuery(id+"F34.imprint","IMPRINT",FACE,{"disambiguationData":[TD([[makeQuery(id+"F34.imprint","IMPRINT",EDGE,{"derivedFrom":sQuery(id+"F34.wireOp",EDGE,"E89")}),1.0]])]});
            extrude(context, id + "F35", {"entities" : qUnion([Q0]), "operationType" : NewBodyOperationType.ADD, "depth" : 4.32 * mm});
        }
        {
            var Q0;
            Q0=makeQuery(id+"F28.opExtrude","CAP_EDGE",EDGE,{"disambiguationData":[OSD([sQuery(id+"F27.wireOp",EDGE,"E74")])],"isStart":false});
            var Q1;
            Q1=makeQuery(id+"F35.opExtrude","CAP_EDGE",EDGE,{"disambiguationData":[OSD([sQuery(id+"F34.wireOp",EDGE,"E89")])],"isStart":false});
            fillet(context, id + "F36", {"entities" : qUnion([Q0, Q1]), "radius" : 0.8 * mm, "tangentPropagation" : true, "allowEdgeOverflow" : false});
        }
        {
            var Q0;
            {var subQ0=sQuery(id+"F21.wireOp",EDGE,"E58.right");Q0=makeQuery(id+"F22.opExtrude","SWEPT_FACE",FACE,{"disambiguationData":[OSD([subQ0]),TDD([makeQuery(id+"F21.imprint","IMPRINT",EDGE,{"disambiguationData":[TD([[makeQuery(id+"F21.imprint","INTERSECT",VERTEX,{"derivedFrom":[sQuery(id+"F21.wireOp",EDGE,"E58.bottom"),subQ0]}),-1.0]])],"derivedFrom":subQ0})])]});}
            var sketch = newSketch(context, id + "F37", { "sketchPlane" : qUnion([Q0])});
            skCircle(sketch, "E91.0", {"center": v(6.8, -6.3) * mm, "radius": 0.56 * mm, "construction": true});
            skCircle(sketch, "E92", {"center": v(6.22, -6.3) * mm, "radius": 0.56 * mm});
            skPoint(sketch, "E92.centerSnap0", {"position": v(6.22, -11.18) * mm});
            skCircle(sketch, "E93", {"center": v(7.37, -6.3) * mm, "radius": 0.56 * mm});
            skCircle(sketch, "E94", {"center": v(5.08, -6.3) * mm, "radius": 0.56 * mm});
            skSolve(sketch);
        }
        {
            var Q0;
            Q0=makeQuery(id+"F37.imprint","IMPRINT",FACE,{"disambiguationData":[TD([[makeQuery(id+"F37.imprint","IMPRINT",EDGE,{"derivedFrom":sQuery(id+"F37.wireOp",EDGE,"E94")}),1.0]])]});
            var Q1;
            Q1=makeQuery(id+"F37.imprint","IMPRINT",FACE,{"disambiguationData":[TD([[makeQuery(id+"F37.imprint","IMPRINT",EDGE,{"derivedFrom":sQuery(id+"F37.wireOp",EDGE,"E92")}),1.0]])]});
            var Q2;
            Q2=makeQuery(id+"F37.imprint","IMPRINT",FACE,{"disambiguationData":[TD([[makeQuery(id+"F37.imprint","IMPRINT",EDGE,{"derivedFrom":sQuery(id+"F37.wireOp",EDGE,"E93")}),1.0]])]});
            extrude(context, id + "F38", {"entities" : qUnion([Q0, Q1, Q2]), "operationType" : NewBodyOperationType.ADD, "depth" : 3.17 * mm});
        }
        {
            var Q0;
            Q0=qCreatedBy(makeId("Front.planeOp"),FACE);
            var sketch = newSketch(context, id + "F39", { "sketchPlane" : qUnion([Q0])});
            skArc(sketch, "E95", {"start": v(-37.82, 30.47) * mm, "mid": v(-41.53, 27.05) * mm, "end": v(-37.82, 23.63) * mm});
            skArc(sketch, "E96", {"start": v(-38.42, 31.57) * mm, "mid": v(-38.1, 31.56) * mm, "end": v(-37.78, 31.57) * mm});
            skArc(sketch, "E97", {"start": v(-36.32, 44.76) * mm, "mid": v(-34.67, 47.69) * mm, "end": v(-36.32, 50.62) * mm});
            skLineSegment(sketch, "E98.0", {"start": v(-26.8, 11.18) * mm, "end": v(-49.4, 11.18) * mm, "construction": true});
            skPoint(sketch, "E99", {"position": v(-38.1, 11.18) * mm});
            skArc(sketch, "E100", {"start": v(-19.58, 25.15) * mm, "mid": v(-17.83, 27.05) * mm, "end": v(-19.58, 28.95) * mm});
            skArc(sketch, "E101", {"start": v(-21.41, 33.1) * mm, "mid": v(-19.68, 34.99) * mm, "end": v(-21.41, 36.89) * mm});
            skArc(sketch, "E102", {"start": v(-19.58, 45.8) * mm, "mid": v(-17.83, 47.69) * mm, "end": v(-19.58, 49.59) * mm});
            skArc(sketch, "E103", {"start": v(-54.73, 49.59) * mm, "mid": v(-56.52, 47.69) * mm, "end": v(-54.73, 45.79) * mm});
            skArc(sketch, "E104", {"start": v(-54.79, 36.89) * mm, "mid": v(-56.52, 34.99) * mm, "end": v(-54.79, 33.1) * mm});
            skArc(sketch, "E105", {"start": v(-39.88, 41.34) * mm, "mid": v(-38.1, 39.56) * mm, "end": v(-36.32, 41.34) * mm});
            skArc(sketch, "E106", {"start": v(-36.32, 54.04) * mm, "mid": v(-38.1, 55.82) * mm, "end": v(-39.88, 54.04) * mm});
            skLineSegment(sketch, "E107", {"start": v(-38.1, 54.04) * mm, "end": v(-38.1, 41.34) * mm, "construction": true});
            skLineSegment(sketch, "E108", {"start": v(-39.88, 44.76) * mm, "end": v(-39.88, 41.34) * mm});
            skLineSegment(sketch, "E109", {"start": v(-36.32, 44.4) * mm, "end": v(-36.32, 41.34) * mm});
            skLineSegment(sketch, "E110", {"start": v(-39.88, 50.62) * mm, "end": v(-39.88, 54.04) * mm});
            skLineSegment(sketch, "E111", {"start": v(-36.32, 50.98) * mm, "end": v(-36.32, 54.04) * mm});
            skArc(sketch, "E112.trimOffspring", {"start": v(-39.88, 50.62) * mm, "mid": v(-39.94, 50.58) * mm, "end": v(-40, 50.55) * mm});
            skLineSegment(sketch, "E113", {"start": v(-54.61, 47.69) * mm, "end": v(-19.74, 47.69) * mm, "construction": true});
            skLineSegment(sketch, "E114", {"start": v(-54.61, 34.99) * mm, "end": v(-21.59, 34.99) * mm, "construction": true});
            skLineSegment(sketch, "E115", {"start": v(-19.58, 49.59) * mm, "end": v(-36.32, 50.98) * mm});
            skLineSegment(sketch, "E116", {"start": v(-19.58, 45.8) * mm, "end": v(-36.32, 44.4) * mm});
            skPoint(sketch, "E117.orphan", {"position": v(-37.82, 51.1) * mm});
            skPoint(sketch, "E118.orphan", {"position": v(-37.82, 44.27) * mm});
            skLineSegment(sketch, "E119", {"start": v(-21.41, 36.89) * mm, "end": v(-37.78, 38.4) * mm});
            skLineSegment(sketch, "E120", {"start": v(-21.41, 33.1) * mm, "end": v(-37.78, 31.57) * mm});
            skLineSegment(sketch, "E121", {"start": v(-38.42, 38.4) * mm, "end": v(-54.79, 36.89) * mm});
            skLineSegment(sketch, "E122", {"start": v(-38.42, 31.57) * mm, "end": v(-54.79, 33.1) * mm});
            skLineSegment(sketch, "E123", {"start": v(-54.73, 49.59) * mm, "end": v(-40, 50.55) * mm});
            skLineSegment(sketch, "E124", {"start": v(-54.73, 45.79) * mm, "end": v(-40, 44.83) * mm});
            skLineSegment(sketch, "E125", {"start": v(-37.82, 30.47) * mm, "end": v(-19.58, 28.95) * mm});
            skLineSegment(sketch, "E126", {"start": v(-19.58, 25.15) * mm, "end": v(-37.82, 23.63) * mm});
            skCircle(sketch, "E127", {"center": v(-38.1, 47.69) * mm, "radius": 1.27 * mm});
            skCircle(sketch, "E128", {"center": v(-38.1, 34.99) * mm, "radius": 1.27 * mm});
            skCircle(sketch, "E129", {"center": v(-38.1, 27.05) * mm, "radius": 1.27 * mm});
            skArc(sketch, "E130.trimOffspring", {"start": v(-37.78, 38.4) * mm, "mid": v(-38.1, 38.42) * mm, "end": v(-38.42, 38.4) * mm});
            skArc(sketch, "E131.trimOffspring", {"start": v(-40, 44.83) * mm, "mid": v(-39.94, 44.8) * mm, "end": v(-39.88, 44.76) * mm});
            skSolve(sketch);
        }
        {
            var Q0;
            Q0=makeQuery(id+"F39.imprint","IMPRINT",FACE,{"disambiguationData":[TD([[makeQuery(id+"F39.imprint","IMPRINT",EDGE,{"derivedFrom":sQuery(id+"F39.wireOp",EDGE,"E102")}),1.0]])]});
            var Q1;
            Q1=makeQuery(id+"F39.imprint","IMPRINT",FACE,{"disambiguationData":[TD([[makeQuery(id+"F39.imprint","IMPRINT",EDGE,{"derivedFrom":sQuery(id+"F39.wireOp",EDGE,"E96")}),1.0]])]});
            var Q2;
            Q2=makeQuery(id+"F39.imprint","IMPRINT",FACE,{"disambiguationData":[TD([[makeQuery(id+"F39.imprint","IMPRINT",EDGE,{"derivedFrom":sQuery(id+"F39.wireOp",EDGE,"E95")}),1.0]])]});
            extrude(context, id + "F40", {"entities" : qUnion([Q0, Q1, Q2]), "depth" : 2.08 * mm});
        }
        {
            var Q0;
            Q0=makeQuery(id+"F40.opExtrude","CAP_FACE",FACE,{"disambiguationData":[OSD([sQuery(id+"F39.wireOp",EDGE,"E102"),sQuery(id+"F39.wireOp",EDGE,"E103"),sQuery(id+"F39.wireOp",EDGE,"E105"),sQuery(id+"F39.wireOp",EDGE,"E106"),sQuery(id+"F39.wireOp",EDGE,"E108"),sQuery(id+"F39.wireOp",EDGE,"E109"),sQuery(id+"F39.wireOp",EDGE,"E110"),sQuery(id+"F39.wireOp",EDGE,"E111"),sQuery(id+"F39.wireOp",EDGE,"E112.trimOffspring"),sQuery(id+"F39.wireOp",EDGE,"E115"),sQuery(id+"F39.wireOp",EDGE,"E116"),sQuery(id+"F39.wireOp",EDGE,"E123"),sQuery(id+"F39.wireOp",EDGE,"E124"),sQuery(id+"F39.wireOp",EDGE,"E127"),sQuery(id+"F39.wireOp",EDGE,"E131.trimOffspring")])],"isStart":true});
            var sketch = newSketch(context, id + "F41", { "sketchPlane" : qUnion([Q0])});
            skCircle(sketch, "E132.0", {"center": v(38.1, 47.69) * mm, "radius": 1.27 * mm, "construction": true});
            skCircle(sketch, "E133.0", {"center": v(38.1, 34.99) * mm, "radius": 1.27 * mm, "construction": true});
            skCircle(sketch, "E134.0", {"center": v(38.1, 27.05) * mm, "radius": 1.27 * mm, "construction": true});
            skCircle(sketch, "E135", {"center": v(38.1, 47.69) * mm, "radius": 3.43 * mm});
            skPoint(sketch, "E136.0", {"position": v(37.78, 38.4) * mm});
            skPoint(sketch, "E137.0", {"position": v(37.82, 30.47) * mm});
            skCircle(sketch, "E138", {"center": v(38.1, 27.05) * mm, "radius": 3.43 * mm});
            skCircle(sketch, "E139", {"center": v(38.1, 34.99) * mm, "radius": 3.43 * mm});
            skCircle(sketch, "E140", {"center": v(38.1, 34.99) * mm, "radius": 2.51 * mm});
            skCircle(sketch, "E141", {"center": v(38.1, 27.05) * mm, "radius": 2.51 * mm});
            skCircle(sketch, "E142", {"center": v(38.1, 47.69) * mm, "radius": 2.51 * mm});
            skSolve(sketch);
        }
        {
            var Q0;
            Q0=makeQuery(id+"F41.imprint","IMPRINT",FACE,{"disambiguationData":[TD([[makeQuery(id+"F41.imprint","IMPRINT",EDGE,{"derivedFrom":sQuery(id+"F41.wireOp",EDGE,"E139")}),1.0]])]});
            var Q1;
            Q1=makeQuery(id+"F41.imprint","IMPRINT",FACE,{"disambiguationData":[TD([[makeQuery(id+"F41.imprint","IMPRINT",EDGE,{"derivedFrom":sQuery(id+"F41.wireOp",EDGE,"E138")}),1.0]])]});
            var Q2;
            Q2=makeQuery(id+"F41.imprint","IMPRINT",FACE,{"disambiguationData":[TD([[makeQuery(id+"F41.imprint","IMPRINT",EDGE,{"derivedFrom":sQuery(id+"F41.wireOp",EDGE,"E142")}),-1.0]])]});
            extrude(context, id + "F42", {"entities" : qUnion([Q0, Q1, Q2]), "operationType" : NewBodyOperationType.ADD, "depth" : 0.46 * mm});
        }
        {
            var Q0;
            Q0=makeQuery(id+"F42.opExtrude","CAP_FACE",FACE,{"disambiguationData":[OSD([sQuery(id+"F41.wireOp",EDGE,"E135"),sQuery(id+"F41.wireOp",EDGE,"E142")])],"isStart":false});
            var sketch = newSketch(context, id + "F43", { "sketchPlane" : qUnion([Q0])});
            skCircle(sketch, "E143.0", {"center": v(38.1, 47.69) * mm, "radius": 2.51 * mm});
            skCircle(sketch, "E144.0", {"center": v(38.1, 34.99) * mm, "radius": 2.51 * mm});
            skCircle(sketch, "E145.0", {"center": v(38.1, 27.05) * mm, "radius": 2.51 * mm});
            skSolve(sketch);
        }
        {
            var Q0;
            Q0=makeQuery(id+"F43.imprint","IMPRINT",FACE,{"disambiguationData":[TD([[makeQuery(id+"F43.imprint","IMPRINT",EDGE,{"derivedFrom":sQuery(id+"F43.wireOp",EDGE,"E143.0")}),1.0]])]});
            var Q1;
            Q1=makeQuery(id+"F43.imprint","IMPRINT",FACE,{"disambiguationData":[TD([[makeQuery(id+"F43.imprint","IMPRINT",EDGE,{"derivedFrom":sQuery(id+"F43.wireOp",EDGE,"E144.0")}),1.0]])]});
            var Q2;
            Q2=makeQuery(id+"F43.imprint","IMPRINT",FACE,{"disambiguationData":[TD([[makeQuery(id+"F43.imprint","IMPRINT",EDGE,{"derivedFrom":sQuery(id+"F43.wireOp",EDGE,"E145.0")}),1.0]])]});
            extrude(context, id + "F44", {"entities" : qUnion([Q0, Q1, Q2]), "operationType" : NewBodyOperationType.REMOVE, "oppositeDirection" : true, "depth" : 1.52 * mm});
        }
        {
            var Q0;
            Q0=makeQuery(id+"F40.opExtrude","CAP_FACE",FACE,{"disambiguationData":[OSD([sQuery(id+"F39.wireOp",EDGE,"E102"),sQuery(id+"F39.wireOp",EDGE,"E103"),sQuery(id+"F39.wireOp",EDGE,"E105"),sQuery(id+"F39.wireOp",EDGE,"E106"),sQuery(id+"F39.wireOp",EDGE,"E108"),sQuery(id+"F39.wireOp",EDGE,"E109"),sQuery(id+"F39.wireOp",EDGE,"E110"),sQuery(id+"F39.wireOp",EDGE,"E111"),sQuery(id+"F39.wireOp",EDGE,"E112.trimOffspring"),sQuery(id+"F39.wireOp",EDGE,"E115"),sQuery(id+"F39.wireOp",EDGE,"E116"),sQuery(id+"F39.wireOp",EDGE,"E123"),sQuery(id+"F39.wireOp",EDGE,"E124"),sQuery(id+"F39.wireOp",EDGE,"E127"),sQuery(id+"F39.wireOp",EDGE,"E131.trimOffspring")])],"isStart":false});
            var sketch = newSketch(context, id + "F45", { "sketchPlane" : qUnion([Q0])});
            skCircle(sketch, "E146.0", {"center": v(-38.1, 47.69) * mm, "radius": 1.27 * mm, "construction": true});
            skCircle(sketch, "E147.0", {"center": v(-38.1, 34.99) * mm, "radius": 1.27 * mm, "construction": true});
            skCircle(sketch, "E148.0", {"center": v(-38.1, 27.05) * mm, "radius": 1.27 * mm, "construction": true});
            skPoint(sketch, "E149.0", {"position": v(-37.82, 30.47) * mm});
            skPoint(sketch, "E150.0", {"position": v(-37.78, 38.4) * mm});
            skCircle(sketch, "E151", {"center": v(-38.1, 47.69) * mm, "radius": 3.43 * mm});
            skCircle(sketch, "E152", {"center": v(-38.1, 34.99) * mm, "radius": 3.43 * mm});
            skCircle(sketch, "E153", {"center": v(-38.1, 27.05) * mm, "radius": 3.43 * mm});
            skCircle(sketch, "E154", {"center": v(-38.1, 34.99) * mm, "radius": 2.2 * mm});
            skCircle(sketch, "E155", {"center": v(-38.1, 47.69) * mm, "radius": 2.2 * mm});
            skCircle(sketch, "E156", {"center": v(-38.1, 27.05) * mm, "radius": 2.2 * mm});
            skSolve(sketch);
        }
        {
            var Q0;
            Q0=makeQuery(id+"F45.imprint","IMPRINT",FACE,{"disambiguationData":[TD([[makeQuery(id+"F45.imprint","IMPRINT",EDGE,{"derivedFrom":sQuery(id+"F45.wireOp",EDGE,"E155")}),-1.0]])]});
            var Q1;
            Q1=makeQuery(id+"F45.imprint","IMPRINT",FACE,{"disambiguationData":[TD([[makeQuery(id+"F45.imprint","IMPRINT",EDGE,{"derivedFrom":sQuery(id+"F45.wireOp",EDGE,"E152")}),1.0]])]});
            var Q2;
            Q2=makeQuery(id+"F45.imprint","IMPRINT",FACE,{"disambiguationData":[TD([[makeQuery(id+"F45.imprint","IMPRINT",EDGE,{"derivedFrom":sQuery(id+"F45.wireOp",EDGE,"E153")}),1.0]])]});
            extrude(context, id + "F46", {"entities" : qUnion([Q0, Q1, Q2]), "operationType" : NewBodyOperationType.ADD, "depth" : 2.7 * mm});
        }
        {
            var Q0;
            Q0=makeQuery(id+"F46.opExtrude","CAP_FACE",FACE,{"disambiguationData":[OSD([sQuery(id+"F45.wireOp",EDGE,"E151"),sQuery(id+"F45.wireOp",EDGE,"E155")])],"isStart":false});
            var sketch = newSketch(context, id + "F47", { "sketchPlane" : qUnion([Q0])});
            skCircle(sketch, "E157.0", {"center": v(-38.1, 47.69) * mm, "radius": 2.2 * mm});
            skCircle(sketch, "E158.0", {"center": v(-38.1, 34.99) * mm, "radius": 2.2 * mm});
            skCircle(sketch, "E159.0", {"center": v(-38.1, 27.05) * mm, "radius": 2.2 * mm});
            skSolve(sketch);
        }
        {
            var Q0;
            Q0=makeQuery(id+"F47.imprint","IMPRINT",FACE,{"disambiguationData":[TD([[makeQuery(id+"F47.imprint","IMPRINT",EDGE,{"derivedFrom":sQuery(id+"F47.wireOp",EDGE,"E157.0")}),1.0]])]});
            var Q1;
            Q1=makeQuery(id+"F47.imprint","IMPRINT",FACE,{"disambiguationData":[TD([[makeQuery(id+"F47.imprint","IMPRINT",EDGE,{"derivedFrom":sQuery(id+"F47.wireOp",EDGE,"E158.0")}),1.0]])]});
            var Q2;
            Q2=makeQuery(id+"F47.imprint","IMPRINT",FACE,{"disambiguationData":[TD([[makeQuery(id+"F47.imprint","IMPRINT",EDGE,{"derivedFrom":sQuery(id+"F47.wireOp",EDGE,"E159.0")}),1.0]])]});
            extrude(context, id + "F48", {"entities" : qUnion([Q0, Q1, Q2]), "operationType" : NewBodyOperationType.REMOVE, "oppositeDirection" : true, "depth" : 2.95 * mm});
        }
        {
            var Q0;
            Q0=qCreatedBy(makeId("Front.planeOp"),FACE);
            var sketch = newSketch(context, id + "F49", { "sketchPlane" : qUnion([Q0])});
            skCircle(sketch, "E160", {"center": v(38.1, 50.8) * mm, "radius": 25.27 * mm});
            skArc(sketch, "E161", {"start": v(14.92, 55.66) * mm, "mid": v(15.57, 43.48) * mm, "end": v(22.2, 33.24) * mm});
            skArc(sketch, "E162", {"start": v(35.21, 41.72) * mm, "mid": v(38.1, 41.28) * mm, "end": v(40.99, 41.72) * mm});
            skLineSegment(sketch, "E163", {"start": v(35.1, 59.84) * mm, "end": v(35.56, 74.35) * mm});
            skLineSegment(sketch, "E164", {"start": v(40.64, 74.35) * mm, "end": v(41.1, 59.84) * mm});
            skCircle(sketch, "E165", {"center": v(38.1, 50.8) * mm, "radius": 1.27 * mm});
            skLineSegment(sketch, "E166", {"start": v(36.9, 63.48) * mm, "end": v(37.19, 71.5) * mm});
            skLineSegment(sketch, "E167", {"start": v(39.01, 71.5) * mm, "end": v(39.3, 63.48) * mm});
            skArc(sketch, "E168", {"start": v(39.01, 71.5) * mm, "mid": v(38.1, 72.4) * mm, "end": v(37.19, 71.5) * mm});
            skArc(sketch, "E169", {"start": v(36.9, 63.48) * mm, "mid": v(38.1, 62.23) * mm, "end": v(39.3, 63.48) * mm});
            skLineSegment(sketch, "E170.1.0", {"start": v(16.49, 60.5) * mm, "end": v(30.43, 56.44) * mm});
            skLineSegment(sketch, "E170.1.1", {"start": v(25.67, 53.57) * mm, "end": v(18.12, 56.33) * mm});
            skLineSegment(sketch, "E170.1.2", {"start": v(28.58, 50.74) * mm, "end": v(14.92, 55.66) * mm});
            skLineSegment(sketch, "E170.1.3", {"start": v(18.69, 58.07) * mm, "end": v(26.41, 55.87) * mm});
            skArc(sketch, "E170.1.4", {"start": v(25.67, 53.57) * mm, "mid": v(27.23, 54.33) * mm, "end": v(26.41, 55.87) * mm});
            skArc(sketch, "E170.1.5", {"start": v(18.69, 58.07) * mm, "mid": v(17.57, 57.47) * mm, "end": v(18.12, 56.33) * mm});
            skLineSegment(sketch, "E170.2.0", {"start": v(22.2, 33.24) * mm, "end": v(30.36, 45.25) * mm});
            skLineSegment(sketch, "E170.2.1", {"start": v(31.62, 39.83) * mm, "end": v(26.67, 33.5) * mm});
            skLineSegment(sketch, "E170.2.2", {"start": v(35.21, 41.72) * mm, "end": v(26.31, 30.26) * mm});
            skLineSegment(sketch, "E170.2.3", {"start": v(25.19, 34.58) * mm, "end": v(29.67, 41.25) * mm});
            skArc(sketch, "E170.2.4", {"start": v(31.62, 39.83) * mm, "mid": v(31.38, 41.55) * mm, "end": v(29.67, 41.25) * mm});
            skArc(sketch, "E170.2.5", {"start": v(25.19, 34.58) * mm, "mid": v(25.4, 33.33) * mm, "end": v(26.67, 33.5) * mm});
            skLineSegment(sketch, "E170.3.0", {"start": v(49.89, 30.26) * mm, "end": v(40.99, 41.72) * mm});
            skLineSegment(sketch, "E170.3.1", {"start": v(46.53, 41.25) * mm, "end": v(51.01, 34.58) * mm});
            skLineSegment(sketch, "E170.3.2", {"start": v(45.84, 45.25) * mm, "end": v(54, 33.24) * mm});
            skLineSegment(sketch, "E170.3.3", {"start": v(49.53, 33.5) * mm, "end": v(44.58, 39.83) * mm});
            skArc(sketch, "E170.3.4", {"start": v(46.53, 41.25) * mm, "mid": v(44.82, 41.55) * mm, "end": v(44.58, 39.83) * mm});
            skArc(sketch, "E170.3.5", {"start": v(49.53, 33.5) * mm, "mid": v(50.8, 33.33) * mm, "end": v(51.01, 34.58) * mm});
            skLineSegment(sketch, "E170.4.0", {"start": v(61.28, 55.66) * mm, "end": v(47.62, 50.74) * mm});
            skLineSegment(sketch, "E170.4.1", {"start": v(49.79, 55.87) * mm, "end": v(57.51, 58.07) * mm});
            skLineSegment(sketch, "E170.4.2", {"start": v(45.77, 56.44) * mm, "end": v(59.71, 60.5) * mm});
            skLineSegment(sketch, "E170.4.3", {"start": v(58.08, 56.33) * mm, "end": v(50.53, 53.57) * mm});
            skArc(sketch, "E170.4.4", {"start": v(49.79, 55.87) * mm, "mid": v(48.97, 54.33) * mm, "end": v(50.53, 53.57) * mm});
            skArc(sketch, "E170.4.5", {"start": v(58.08, 56.33) * mm, "mid": v(58.63, 57.47) * mm, "end": v(57.51, 58.07) * mm});
            skArc(sketch, "E171.trimOffspring", {"start": v(35.56, 74.35) * mm, "mid": v(24.18, 69.96) * mm, "end": v(16.49, 60.5) * mm});
            skArc(sketch, "E172.trimOffspring", {"start": v(59.71, 60.5) * mm, "mid": v(52.02, 69.96) * mm, "end": v(40.64, 74.35) * mm});
            skArc(sketch, "E173.trimOffspring", {"start": v(54, 33.24) * mm, "mid": v(60.63, 43.48) * mm, "end": v(61.28, 55.66) * mm});
            skArc(sketch, "E174.trimOffspring", {"start": v(26.31, 30.26) * mm, "mid": v(38.1, 27.11) * mm, "end": v(49.89, 30.26) * mm});
            skArc(sketch, "E175.trimOffspring", {"start": v(28.58, 50.74) * mm, "mid": v(29.04, 47.86) * mm, "end": v(30.36, 45.25) * mm});
            skArc(sketch, "E176.trimOffspring", {"start": v(35.1, 59.84) * mm, "mid": v(32.5, 58.5) * mm, "end": v(30.43, 56.44) * mm});
            skArc(sketch, "E177.trimOffspring", {"start": v(45.77, 56.44) * mm, "mid": v(43.7, 58.5) * mm, "end": v(41.1, 59.84) * mm});
            skArc(sketch, "E178.trimOffspring", {"start": v(45.84, 45.25) * mm, "mid": v(47.16, 47.86) * mm, "end": v(47.62, 50.74) * mm});
            skCircle(sketch, "E179", {"center": v(38.1, 57.15) * mm, "radius": 1.52 * mm});
            skCircle(sketch, "E180", {"center": v(38.1, 44.45) * mm, "radius": 1.52 * mm});
            skCircle(sketch, "E181", {"center": v(31.75, 50.8) * mm, "radius": 1.52 * mm});
            skCircle(sketch, "E182", {"center": v(44.45, 50.8) * mm, "radius": 1.52 * mm});
            skLineSegment(sketch, "E183", {"start": v(31.75, 50.8) * mm, "end": v(44.45, 50.8) * mm, "construction": true});
            skLineSegment(sketch, "E184", {"start": v(38.1, 57.15) * mm, "end": v(38.1, 44.45) * mm, "construction": true});
            skSolve(sketch);
        }
        {
            var Q0;
            Q0=makeQuery(id+"F49.imprint","IMPRINT",FACE,{"disambiguationData":[TD([[makeQuery(id+"F49.imprint","IMPRINT",EDGE,{"derivedFrom":sQuery(id+"F49.wireOp",EDGE,"E160")}),1.0]])]});
            var Q1;
            Q1=makeQuery(id+"F49.imprint","IMPRINT",FACE,{"disambiguationData":[TD([[makeQuery(id+"F49.imprint","IMPRINT",EDGE,{"derivedFrom":sQuery(id+"F49.wireOp",EDGE,"E179")}),1.0]])]});
            var Q2;
            Q2=makeQuery(id+"F49.imprint","IMPRINT",FACE,{"disambiguationData":[TD([[makeQuery(id+"F49.imprint","IMPRINT",EDGE,{"derivedFrom":sQuery(id+"F49.wireOp",EDGE,"E180")}),1.0]])]});
            extrude(context, id + "F50", {"entities" : qUnion([Q0, Q1, Q2]), "depth" : 4.32 * mm});
        }
        {
            var Q0;
            Q0=makeQuery(id+"F50.opExtrude","CAP_FACE",FACE,{"disambiguationData":[OSD([sQuery(id+"F49.wireOp",EDGE,"E160"),sQuery(id+"F49.wireOp",EDGE,"E161"),sQuery(id+"F49.wireOp",EDGE,"E162"),sQuery(id+"F49.wireOp",EDGE,"E163"),sQuery(id+"F49.wireOp",EDGE,"E164"),sQuery(id+"F49.wireOp",EDGE,"E165"),sQuery(id+"F49.wireOp",EDGE,"E166"),sQuery(id+"F49.wireOp",EDGE,"E167"),sQuery(id+"F49.wireOp",EDGE,"E168"),sQuery(id+"F49.wireOp",EDGE,"E169"),sQuery(id+"F49.wireOp",EDGE,"E170.1.0"),sQuery(id+"F49.wireOp",EDGE,"E170.1.1"),sQuery(id+"F49.wireOp",EDGE,"E170.1.2"),sQuery(id+"F49.wireOp",EDGE,"E170.1.3"),sQuery(id+"F49.wireOp",EDGE,"E170.1.4"),sQuery(id+"F49.wireOp",EDGE,"E170.1.5"),sQuery(id+"F49.wireOp",EDGE,"E170.2.0"),sQuery(id+"F49.wireOp",EDGE,"E170.2.1"),sQuery(id+"F49.wireOp",EDGE,"E170.2.2"),sQuery(id+"F49.wireOp",EDGE,"E170.2.3"),sQuery(id+"F49.wireOp",EDGE,"E170.2.4"),sQuery(id+"F49.wireOp",EDGE,"E170.2.5"),sQuery(id+"F49.wireOp",EDGE,"E170.3.0"),sQuery(id+"F49.wireOp",EDGE,"E170.3.1"),sQuery(id+"F49.wireOp",EDGE,"E170.3.2"),sQuery(id+"F49.wireOp",EDGE,"E170.3.3"),sQuery(id+"F49.wireOp",EDGE,"E170.3.4"),sQuery(id+"F49.wireOp",EDGE,"E170.3.5"),sQuery(id+"F49.wireOp",EDGE,"E170.4.0"),sQuery(id+"F49.wireOp",EDGE,"E170.4.1"),sQuery(id+"F49.wireOp",EDGE,"E170.4.2"),sQuery(id+"F49.wireOp",EDGE,"E170.4.3"),sQuery(id+"F49.wireOp",EDGE,"E170.4.4"),sQuery(id+"F49.wireOp",EDGE,"E170.4.5"),sQuery(id+"F49.wireOp",EDGE,"E171.trimOffspring"),sQuery(id+"F49.wireOp",EDGE,"E172.trimOffspring"),sQuery(id+"F49.wireOp",EDGE,"E173.trimOffspring"),sQuery(id+"F49.wireOp",EDGE,"E174.trimOffspring"),sQuery(id+"F49.wireOp",EDGE,"E175.trimOffspring"),sQuery(id+"F49.wireOp",EDGE,"E176.trimOffspring"),sQuery(id+"F49.wireOp",EDGE,"E177.trimOffspring"),sQuery(id+"F49.wireOp",EDGE,"E178.trimOffspring"),sQuery(id+"F49.wireOp",EDGE,"E181"),sQuery(id+"F49.wireOp",EDGE,"E182")])],"isStart":false});
            var sketch = newSketch(context, id + "F51", { "sketchPlane" : qUnion([Q0])});
            skCircle(sketch, "E185.0", {"center": v(38.1, 57.15) * mm, "radius": 1.52 * mm});
            skCircle(sketch, "E186.0", {"center": v(38.1, 44.45) * mm, "radius": 1.52 * mm});
            skSolve(sketch);
        }
        {
            var Q0;
            Q0=makeQuery(id+"F51.imprint","IMPRINT",FACE,{"disambiguationData":[TD([[makeQuery(id+"F51.imprint","IMPRINT",EDGE,{"derivedFrom":sQuery(id+"F51.wireOp",EDGE,"E185.0")}),1.0]])]});
            var Q1;
            Q1=makeQuery(id+"F51.imprint","IMPRINT",FACE,{"disambiguationData":[TD([[makeQuery(id+"F51.imprint","IMPRINT",EDGE,{"derivedFrom":sQuery(id+"F51.wireOp",EDGE,"E186.0")}),1.0]])]});
            extrude(context, id + "F52", {"entities" : qUnion([Q0, Q1]), "operationType" : NewBodyOperationType.REMOVE, "oppositeDirection" : true, "depth" : 2.54 * mm});
        }
        {
            var Q0;
            Q0=makeQuery(id+"F50.opExtrude","CAP_FACE",FACE,{"disambiguationData":[OSD([sQuery(id+"F49.wireOp",EDGE,"E160"),sQuery(id+"F49.wireOp",EDGE,"E161"),sQuery(id+"F49.wireOp",EDGE,"E162"),sQuery(id+"F49.wireOp",EDGE,"E163"),sQuery(id+"F49.wireOp",EDGE,"E164"),sQuery(id+"F49.wireOp",EDGE,"E165"),sQuery(id+"F49.wireOp",EDGE,"E166"),sQuery(id+"F49.wireOp",EDGE,"E167"),sQuery(id+"F49.wireOp",EDGE,"E168"),sQuery(id+"F49.wireOp",EDGE,"E169"),sQuery(id+"F49.wireOp",EDGE,"E170.1.0"),sQuery(id+"F49.wireOp",EDGE,"E170.1.1"),sQuery(id+"F49.wireOp",EDGE,"E170.1.2"),sQuery(id+"F49.wireOp",EDGE,"E170.1.3"),sQuery(id+"F49.wireOp",EDGE,"E170.1.4"),sQuery(id+"F49.wireOp",EDGE,"E170.1.5"),sQuery(id+"F49.wireOp",EDGE,"E170.2.0"),sQuery(id+"F49.wireOp",EDGE,"E170.2.1"),sQuery(id+"F49.wireOp",EDGE,"E170.2.2"),sQuery(id+"F49.wireOp",EDGE,"E170.2.3"),sQuery(id+"F49.wireOp",EDGE,"E170.2.4"),sQuery(id+"F49.wireOp",EDGE,"E170.2.5"),sQuery(id+"F49.wireOp",EDGE,"E170.3.0"),sQuery(id+"F49.wireOp",EDGE,"E170.3.1"),sQuery(id+"F49.wireOp",EDGE,"E170.3.2"),sQuery(id+"F49.wireOp",EDGE,"E170.3.3"),sQuery(id+"F49.wireOp",EDGE,"E170.3.4"),sQuery(id+"F49.wireOp",EDGE,"E170.3.5"),sQuery(id+"F49.wireOp",EDGE,"E170.4.0"),sQuery(id+"F49.wireOp",EDGE,"E170.4.1"),sQuery(id+"F49.wireOp",EDGE,"E170.4.2"),sQuery(id+"F49.wireOp",EDGE,"E170.4.3"),sQuery(id+"F49.wireOp",EDGE,"E170.4.4"),sQuery(id+"F49.wireOp",EDGE,"E170.4.5"),sQuery(id+"F49.wireOp",EDGE,"E171.trimOffspring"),sQuery(id+"F49.wireOp",EDGE,"E172.trimOffspring"),sQuery(id+"F49.wireOp",EDGE,"E173.trimOffspring"),sQuery(id+"F49.wireOp",EDGE,"E174.trimOffspring"),sQuery(id+"F49.wireOp",EDGE,"E175.trimOffspring"),sQuery(id+"F49.wireOp",EDGE,"E176.trimOffspring"),sQuery(id+"F49.wireOp",EDGE,"E177.trimOffspring"),sQuery(id+"F49.wireOp",EDGE,"E178.trimOffspring"),sQuery(id+"F49.wireOp",EDGE,"E181"),sQuery(id+"F49.wireOp",EDGE,"E182")])],"isStart":false});
            var sketch = newSketch(context, id + "F53", { "sketchPlane" : qUnion([Q0])});
            skCircle(sketch, "E187", {"center": v(38.1, 50.8) * mm, "radius": 3.48 * mm});
            skCircle(sketch, "E188", {"center": v(38.1, 50.8) * mm, "radius": 2.2 * mm});
            skSolve(sketch);
        }
        {
            var Q0;
            Q0=makeQuery(id+"F53.imprint","IMPRINT",FACE,{"disambiguationData":[TD([[makeQuery(id+"F53.imprint","IMPRINT",EDGE,{"derivedFrom":sQuery(id+"F53.wireOp",EDGE,"E187")}),1.0]])]});
            extrude(context, id + "F54", {"entities" : qUnion([Q0]), "operationType" : NewBodyOperationType.ADD, "depth" : 1.17 * mm});
        }
        {
            var Q0;
            Q0=makeQuery(id+"F54.opExtrude","CAP_FACE",FACE,{"disambiguationData":[OSD([sQuery(id+"F53.wireOp",EDGE,"E187"),sQuery(id+"F53.wireOp",EDGE,"E188")])],"isStart":false});
            var sketch = newSketch(context, id + "F55", { "sketchPlane" : qUnion([Q0])});
            skCircle(sketch, "E189.0", {"center": v(38.1, 50.8) * mm, "radius": 2.2 * mm});
            skSolve(sketch);
        }
        {
            var Q0;
            Q0=makeQuery(id+"F55.imprint","IMPRINT",FACE,{"disambiguationData":[TD([[makeQuery(id+"F55.imprint","IMPRINT",EDGE,{"derivedFrom":sQuery(id+"F55.wireOp",EDGE,"E189.0")}),1.0]])]});
            extrude(context, id + "F56", {"entities" : qUnion([Q0]), "operationType" : NewBodyOperationType.REMOVE, "oppositeDirection" : true, "depth" : 2.54 * mm});
        }
        {
            var Q0;
            {var subQ0=sQuery(id+"F49.wireOp",EDGE,"E170.2.5");var subQ1=sQuery(id+"F49.wireOp",EDGE,"E174.trimOffspring");var subQ2=sQuery(id+"F49.wireOp",EDGE,"E170.3.0");var subQ3=sQuery(id+"F49.wireOp",EDGE,"E175.trimOffspring");var subQ4=sQuery(id+"F49.wireOp",EDGE,"E170.2.4");var subQ5=sQuery(id+"F49.wireOp",EDGE,"E173.trimOffspring");var subQ6=sQuery(id+"F49.wireOp",EDGE,"E170.2.3");var subQ7=sQuery(id+"F49.wireOp",EDGE,"E172.trimOffspring");var subQ8=sQuery(id+"F49.wireOp",EDGE,"E170.2.2");var subQ9=sQuery(id+"F49.wireOp",EDGE,"E171.trimOffspring");var subQ10=sQuery(id+"F49.wireOp",EDGE,"E170.2.1");var subQ11=sQuery(id+"F49.wireOp",EDGE,"E170.4.5");var subQ12=sQuery(id+"F49.wireOp",EDGE,"E170.2.0");var subQ13=sQuery(id+"F49.wireOp",EDGE,"E170.4.4");var subQ14=sQuery(id+"F49.wireOp",EDGE,"E170.1.5");var subQ15=sQuery(id+"F49.wireOp",EDGE,"E170.4.3");var subQ16=sQuery(id+"F49.wireOp",EDGE,"E170.1.3");var subQ17=sQuery(id+"F49.wireOp",EDGE,"E170.4.1");var subQ18=sQuery(id+"F49.wireOp",EDGE,"E170.1.4");var subQ19=sQuery(id+"F49.wireOp",EDGE,"E170.4.2");var subQ20=sQuery(id+"F49.wireOp",EDGE,"E170.1.2");var subQ21=sQuery(id+"F49.wireOp",EDGE,"E170.1.1");var subQ22=sQuery(id+"F49.wireOp",EDGE,"E163");var subQ23=sQuery(id+"F49.wireOp",EDGE,"E170.4.0");var subQ24=sQuery(id+"F49.wireOp",EDGE,"E170.1.0");var subQ25=sQuery(id+"F49.wireOp",EDGE,"E162");var subQ26=sQuery(id+"F49.wireOp",EDGE,"E170.3.5");var subQ27=sQuery(id+"F49.wireOp",EDGE,"E182");var subQ28=sQuery(id+"F49.wireOp",EDGE,"E169");var subQ29=sQuery(id+"F49.wireOp",EDGE,"E161");var subQ30=sQuery(id+"F49.wireOp",EDGE,"E170.3.4");var subQ31=sQuery(id+"F49.wireOp",EDGE,"E181");var subQ32=sQuery(id+"F49.wireOp",EDGE,"E168");var subQ33=sQuery(id+"F49.wireOp",EDGE,"E160");var subQ34=sQuery(id+"F49.wireOp",EDGE,"E170.3.1");var subQ35=sQuery(id+"F49.wireOp",EDGE,"E176.trimOffspring");var subQ36=sQuery(id+"F49.wireOp",EDGE,"E164");var subQ37=sQuery(id+"F49.wireOp",EDGE,"E166");var subQ38=sQuery(id+"F49.wireOp",EDGE,"E167");var subQ39=sQuery(id+"F49.wireOp",EDGE,"E170.3.2");var subQ40=sQuery(id+"F49.wireOp",EDGE,"E177.trimOffspring");var subQ41=sQuery(id+"F49.wireOp",EDGE,"E170.3.3");var subQ42=sQuery(id+"F49.wireOp",EDGE,"E178.trimOffspring");Q0=makeQuery(id+"F54.boolean.opBoolean","SPLIT",FACE,{"disambiguationData":[TD([makeQuery(id+"F50.opExtrude","SWEPT_FACE",FACE,{"disambiguationData":[OSD([subQ33])]})])],"derivedFrom":makeQuery(id+"F50.opExtrude","CAP_FACE",FACE,{"disambiguationData":[OSD([subQ33,subQ29,subQ25,subQ22,subQ36,sQuery(id+"F49.wireOp",EDGE,"E165"),subQ37,subQ38,subQ32,subQ28,subQ24,subQ21,subQ20,subQ16,subQ18,subQ14,subQ12,subQ10,subQ8,subQ6,subQ4,subQ0,subQ2,subQ34,subQ39,subQ41,subQ30,subQ26,subQ23,subQ17,subQ19,subQ15,subQ13,subQ11,subQ9,subQ7,subQ5,subQ1,subQ3,subQ35,subQ40,subQ42,subQ31,subQ27])],"isStart":false})});}
            var sketch = newSketch(context, id + "F57", { "sketchPlane" : qUnion([Q0])});
            skCircle(sketch, "E190", {"center": v(38.1, 50.8) * mm, "radius": 23.69 * mm});
            skSolve(sketch);
        }
        {
            var Q0;
            Q0=makeQuery(id+"F57.imprint","IMPRINT",FACE,{"disambiguationData":[TD([[makeQuery(id+"F57.imprint","IMPRINT",EDGE,{"derivedFrom":makeQuery(id+"F50.opExtrude","CAP_EDGE",EDGE,{"disambiguationData":[OSD([sQuery(id+"F49.wireOp",EDGE,"E160")])],"isStart":false})}),1.0]])]});
            extrude(context, id + "F58", {"entities" : qUnion([Q0]), "operationType" : NewBodyOperationType.ADD, "depth" : 1.84 * mm, "hasSecondDirection" : true, "secondDirectionOppositeDirection" : true, "secondDirectionDepth" : 6.16 * mm});
        }
        {
            var Q0;
            Q0=makeQuery(id+"F58.opExtrude","CAP_FACE",FACE,{"disambiguationData":[OSD([sQuery(id+"F49.wireOp",EDGE,"E160"),sQuery(id+"F57.wireOp",EDGE,"E190")])],"isStart":false});
            var sketch = newSketch(context, id + "F59", { "sketchPlane" : qUnion([Q0])});
            skCircle(sketch, "E191", {"center": v(38.1, 50.8) * mm, "radius": 30.35 * mm});
            skCircle(sketch, "E192", {"center": v(38.1, 50.8) * mm, "radius": 25.78 * mm});
            skSolve(sketch);
        }
        {
            var Q0;
            Q0=makeQuery(id+"F59.imprint","IMPRINT",FACE,{"disambiguationData":[TD([[makeQuery(id+"F59.imprint","IMPRINT",EDGE,{"derivedFrom":sQuery(id+"F59.wireOp",EDGE,"E191")}),1.0]])]});
            extrude(context, id + "F60", {"entities" : qUnion([Q0]), "oppositeDirection" : true, "depth" : 8 * mm});
        }
        {
            var Q0;
            Q0=makeQuery(id+"F59.imprint","IMPRINT",FACE,{"disambiguationData":[TD([[makeQuery(id+"F59.imprint","IMPRINT",EDGE,{"derivedFrom":sQuery(id+"F59.wireOp",EDGE,"E192")}),1.0]])]});
            extrude(context, id + "F61", {"entities" : qUnion([Q0]), "operationType" : NewBodyOperationType.ADD, "oppositeDirection" : true, "depth" : 7.5 * mm, "hasSecondDirection" : true, "secondDirectionOppositeDirection" : true, "secondDirectionDepth" : 0.5 * mm});
        }
    });
